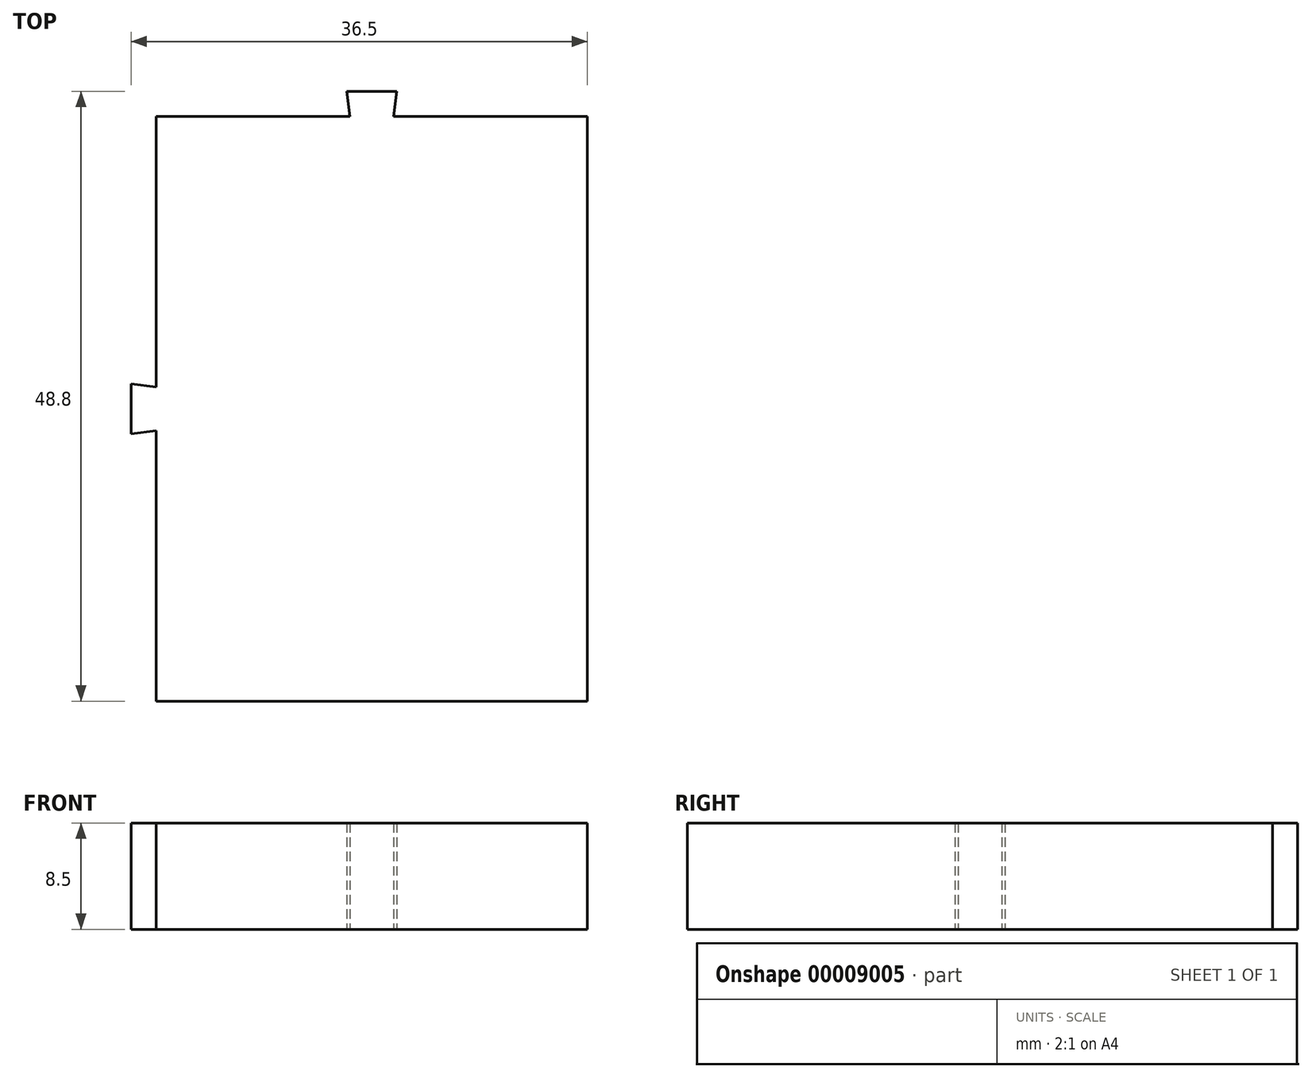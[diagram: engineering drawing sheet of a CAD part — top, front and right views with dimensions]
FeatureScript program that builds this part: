
annotation { "Feature Type Name" : "Feature", "Feature Type Description" : "" }
export const myFeature = defineFeature(function(context is Context, id is Id, definition is map)
    precondition{}
    {
        {
            var Q0;
            Q0=qCreatedBy(makeId("Top.planeOp"),FACE);
            var sketch = newSketch(context, id + "F0", { "sketchPlane" : qUnion([Q0])});
            skLineSegment(sketch, "E0", {"start": v(0, 0) * mm, "end": v(34.5, 0) * mm});
            skLineSegment(sketch, "E1", {"start": v(34.5, 0) * mm, "end": v(34.5, 46.8) * mm});
            skLineSegment(sketch, "E2", {"start": v(34.5, 46.8) * mm, "end": v(19, 46.8) * mm});
            skLineSegment(sketch, "E3", {"start": v(19.25, 48.8) * mm, "end": v(15.25, 48.8) * mm});
            skLineSegment(sketch, "E4", {"start": v(15.25, 48.8) * mm, "end": v(15.5, 46.8) * mm});
            skLineSegment(sketch, "E5", {"start": v(15.5, 46.8) * mm, "end": v(0, 46.8) * mm});
            skLineSegment(sketch, "E6", {"start": v(0, 46.8) * mm, "end": v(0, 25.15) * mm});
            skLineSegment(sketch, "E7", {"start": v(-2, 25.4) * mm, "end": v(-2, 21.4) * mm});
            skLineSegment(sketch, "E8", {"start": v(-2, 21.4) * mm, "end": v(0, 21.65) * mm});
            skLineSegment(sketch, "E9", {"start": v(0, 21.65) * mm, "end": v(0, 0) * mm});
            skLineSegment(sketch, "E10", {"start": v(15.5, 46.8) * mm, "end": v(19, 46.8) * mm, "construction": true});
            skLineSegment(sketch, "E11", {"start": v(0, 25.15) * mm, "end": v(0, 21.65) * mm, "construction": true});
            skLineSegment(sketch, "E12", {"start": v(19.25, 48.8) * mm, "end": v(19, 46.8) * mm});
            skLineSegment(sketch, "E13", {"start": v(-2, 25.4) * mm, "end": v(0, 25.15) * mm});
            skSolve(sketch);
        }
        {
            var Q0;
            Q0=makeQuery(id+"F0.imprint","IMPRINT",FACE,{"disambiguationData":[TD([[makeQuery(id+"F0.imprint","IMPRINT",EDGE,{"derivedFrom":sQuery(id+"F0.wireOp",EDGE,"E0")}),1.0]])]});
            extrude(context, id + "F1", {"entities" : qUnion([Q0]), "depth" : 8.5 * mm});
        }
    });
